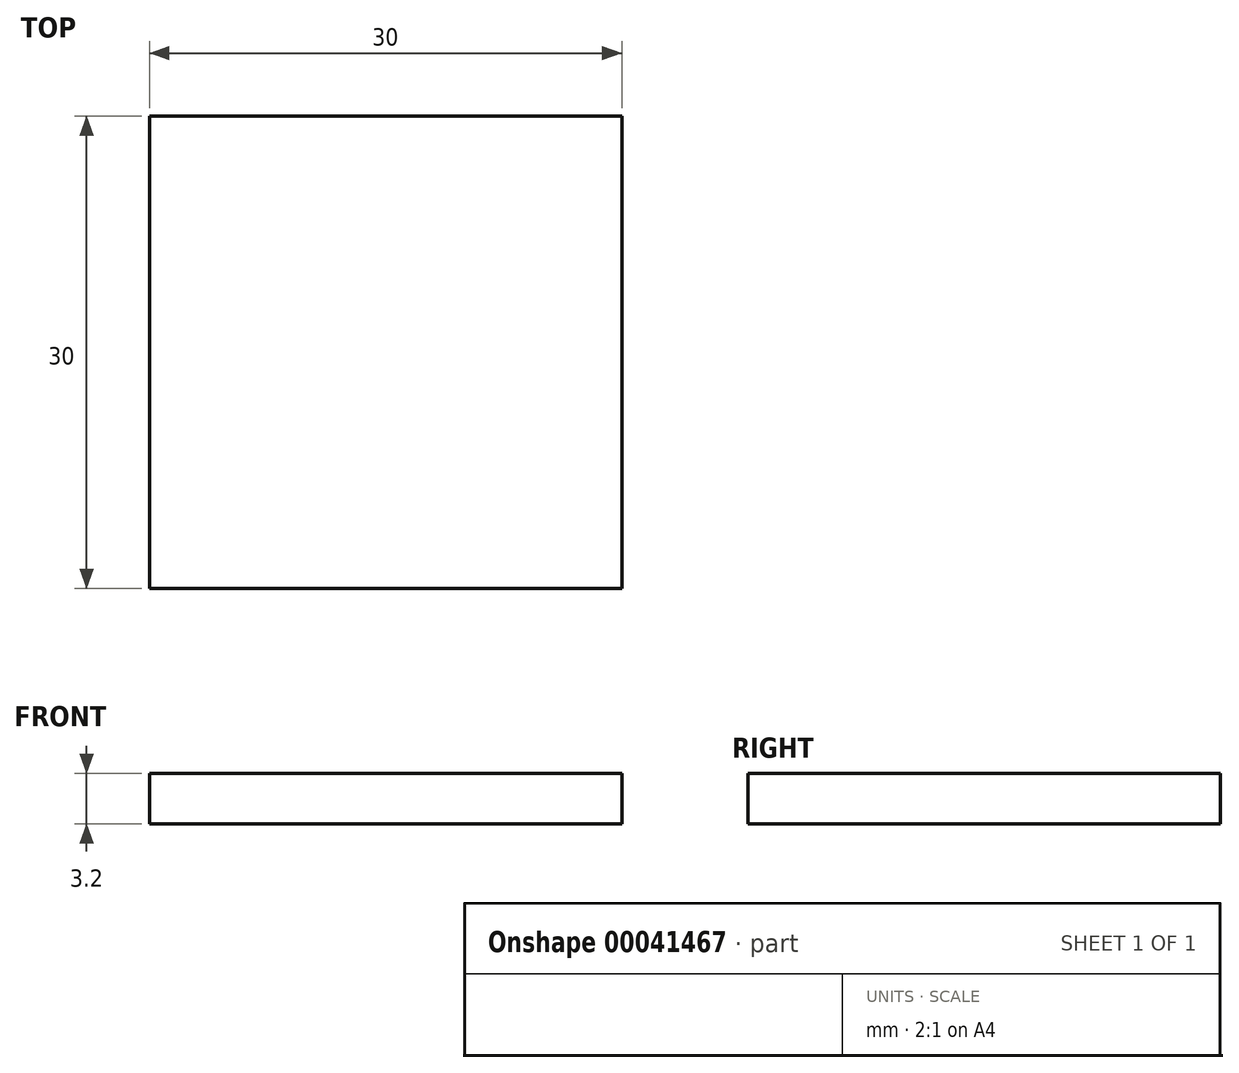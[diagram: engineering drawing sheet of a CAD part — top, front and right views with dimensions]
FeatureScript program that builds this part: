
annotation { "Feature Type Name" : "Feature", "Feature Type Description" : "" }
export const myFeature = defineFeature(function(context is Context, id is Id, definition is map)
    precondition{}
    {
        {
            var Q0;
            Q0=qCreatedBy(makeId("Top.planeOp"),FACE);
            var sketch = newSketch(context, id + "F0", { "sketchPlane" : qUnion([Q0])});
            skLineSegment(sketch, "E0.rect.bottom", {"start": v(15, -15) * mm, "end": v(-15, -15) * mm});
            skLineSegment(sketch, "E0.rect.top", {"start": v(15, 15) * mm, "end": v(-15, 15) * mm});
            skLineSegment(sketch, "E0.rect.left", {"start": v(15, -15) * mm, "end": v(15, 15) * mm});
            skLineSegment(sketch, "E0.rect.right", {"start": v(-15, -15) * mm, "end": v(-15, 15) * mm});
            skPoint(sketch, "E0.rect.middle", {"position": v(0, 0) * mm});
            skSolve(sketch);
        }
        {
            var Q0;
            Q0=makeQuery(id+"F0.imprint","IMPRINT",FACE,{"disambiguationData":[TD([[makeQuery(id+"F0.imprint","IMPRINT",EDGE,{"derivedFrom":sQuery(id+"F0.wireOp",EDGE,"E0.rect.bottom")}),-1.0]])]});
            extrude(context, id + "F1", {"entities" : qUnion([Q0]), "depth" : 3.2 * mm});
        }
    });
